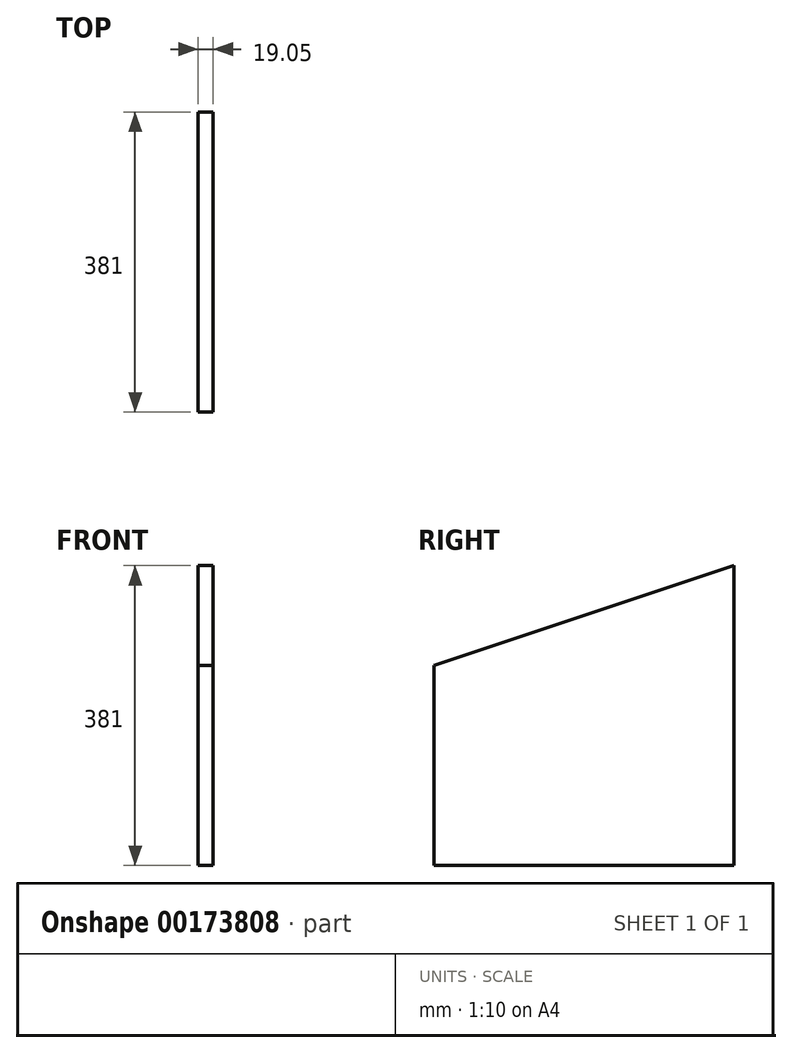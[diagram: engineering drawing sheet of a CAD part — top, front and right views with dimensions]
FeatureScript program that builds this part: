
annotation { "Feature Type Name" : "Feature", "Feature Type Description" : "" }
export const myFeature = defineFeature(function(context is Context, id is Id, definition is map)
    precondition{}
    {
        {
            var Q0;
            Q0=qCreatedBy(makeId("Right.planeOp"),FACE);
            var sketch = newSketch(context, id + "F0", { "sketchPlane" : qUnion([Q0])});
            skLineSegment(sketch, "E0", {"start": v(0, 0) * mm, "end": v(0, 254) * mm});
            skLineSegment(sketch, "E1", {"start": v(0, 254) * mm, "end": v(381, 381) * mm});
            skLineSegment(sketch, "E2", {"start": v(381, 381) * mm, "end": v(381, 0) * mm});
            skLineSegment(sketch, "E3", {"start": v(381, 0) * mm, "end": v(0, 0) * mm});
            skSolve(sketch);
        }
        {
            var Q0;
            Q0 = qSketchRegion(id + "F0", true);
            extrude(context, id + "F1", {"entities" : qUnion([Q0]), "depth" : 19.05 * mm});
        }
    });
